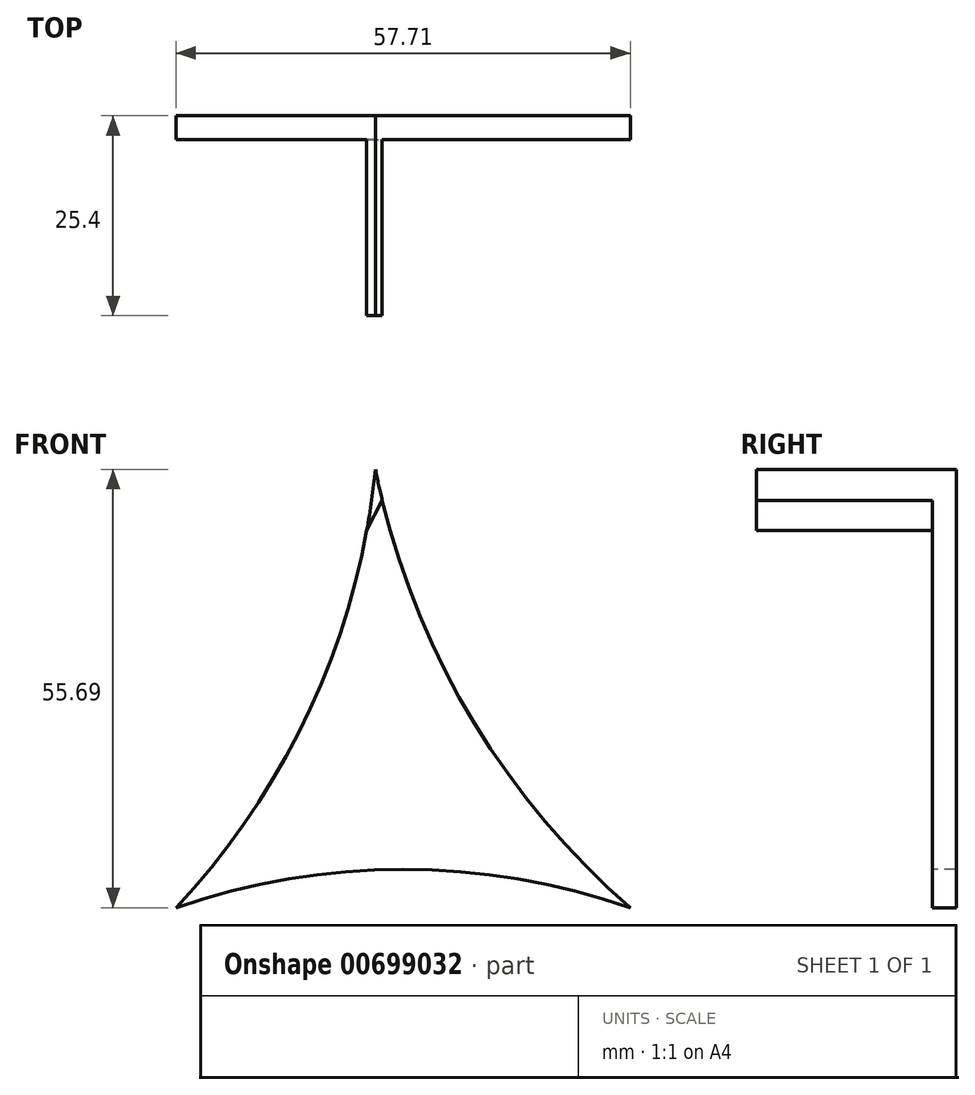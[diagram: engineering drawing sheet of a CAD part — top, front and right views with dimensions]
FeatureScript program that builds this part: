
annotation { "Feature Type Name" : "Feature", "Feature Type Description" : "" }
export const myFeature = defineFeature(function(context is Context, id is Id, definition is map)
    precondition{}
    {
        {
            var Q0;
            Q0=qCreatedBy(makeId("Front.planeOp"),FACE);
            var sketch = newSketch(context, id + "F0", { "sketchPlane" : qUnion([Q0])});
            skLineSegment(sketch, "E0", {"start": v(0, 0) * mm, "end": v(-58, 0) * mm});
            skLineSegment(sketch, "E1", {"start": v(-58, 0) * mm, "end": v(-29.79, 55.11) * mm});
            skLineSegment(sketch, "E2", {"start": v(-29.79, 55.11) * mm, "end": v(0, 0) * mm});
            skSolve(sketch);
        }
        {
            var Q0;
            Q0 = qSketchRegion(id + "F0", true);
            extrude(context, id + "F1", {"entities" : qUnion([Q0]), "depth" : 25.4 * mm, "offsetDistance" : 25.4 * mm});
        }
        {
            var Q0;
            Q0=makeQuery(id+"F0.imprint","IMPRINT",FACE,{"disambiguationData":[TD([[makeQuery(id+"F0.imprint","IMPRINT",EDGE,{"derivedFrom":sQuery(id+"F0.wireOp",EDGE,"E0")}),-1.0]])]});
            var sketch = newSketch(context, id + "F2", { "sketchPlane" : qUnion([Q0])});
            skArc(sketch, "E3", {"start": v(-57.7, 0) * mm, "mid": v(-40.44, 25.75) * mm, "end": v(-32.38, 55.7) * mm});
            skArc(sketch, "E4", {"start": v(-32.38, 55.7) * mm, "mid": v(-20.83, 25.15) * mm, "end": v(0, 0) * mm});
            skArc(sketch, "E5", {"start": v(0, 0) * mm, "mid": v(-28.85, 4.87) * mm, "end": v(-57.7, 0) * mm});
            skSolve(sketch);
        }
        {
            var Q0;
            Q0 = qSketchRegion(id + "F2", true);
            extrude(context, id + "F3", {"entities" : qUnion([Q0]), "operationType" : NewBodyOperationType.ADD, "oppositeDirection" : true, "depth" : 25.4 * mm, "offsetDistance" : 25.4 * mm});
        }
        {
            var Q0;
            {var subQ0=sQuery(id+"F0.wireOp",EDGE,"E2");var subQ1=sQuery(id+"F0.wireOp",EDGE,"E1");var subQ2=sQuery(id+"F0.wireOp",EDGE,"E0");var subQ3=makeQuery(id+"F1.opExtrude","CAP_FACE",FACE,{"disambiguationData":[OSD([subQ2,subQ1,subQ0])],"isStart":true});Q0=makeQuery(id+"F3.boolean.opBoolean","SPLIT",FACE,{"disambiguationData":[TD([makeQuery(id+"F1.opExtrude","SWEPT_FACE",FACE,{"disambiguationData":[OSD([subQ2])]}),subQ3,makeQuery(id+"F1.opExtrude","SWEPT_FACE",FACE,{"disambiguationData":[OSD([subQ1])]}),makeQuery(id+"F1.opExtrude","SWEPT_FACE",FACE,{"disambiguationData":[OSD([subQ0])]}),makeQuery(id+"F3.opExtrude","SWEPT_FACE",FACE,{"disambiguationData":[OSD([sQuery(id+"F2.wireOp",EDGE,"E3")])]}),makeQuery(id+"F3.opExtrude","SWEPT_FACE",FACE,{"disambiguationData":[OSD([sQuery(id+"F2.wireOp",EDGE,"E4")])]}),makeQuery(id+"F3.opExtrude","SWEPT_FACE",FACE,{"disambiguationData":[OSD([sQuery(id+"F2.wireOp",EDGE,"E5")])]})]),OD(0.0)],"derivedFrom":subQ3});}
            var Q1;
            {var subQ0=sQuery(id+"F0.wireOp",EDGE,"E2");var subQ1=sQuery(id+"F0.wireOp",EDGE,"E1");var subQ2=sQuery(id+"F0.wireOp",EDGE,"E0");var subQ3=makeQuery(id+"F1.opExtrude","CAP_FACE",FACE,{"disambiguationData":[OSD([subQ2,subQ1,subQ0])],"isStart":true});Q1=makeQuery(id+"F3.boolean.opBoolean","SPLIT",FACE,{"disambiguationData":[TD([makeQuery(id+"F1.opExtrude","SWEPT_FACE",FACE,{"disambiguationData":[OSD([subQ2])]}),subQ3,makeQuery(id+"F1.opExtrude","SWEPT_FACE",FACE,{"disambiguationData":[OSD([subQ1])]}),makeQuery(id+"F1.opExtrude","SWEPT_FACE",FACE,{"disambiguationData":[OSD([subQ0])]}),makeQuery(id+"F3.opExtrude","SWEPT_FACE",FACE,{"disambiguationData":[OSD([sQuery(id+"F2.wireOp",EDGE,"E3")])]}),makeQuery(id+"F3.opExtrude","SWEPT_FACE",FACE,{"disambiguationData":[OSD([sQuery(id+"F2.wireOp",EDGE,"E4")])]}),makeQuery(id+"F3.opExtrude","SWEPT_FACE",FACE,{"disambiguationData":[OSD([sQuery(id+"F2.wireOp",EDGE,"E5")])]})]),OD(1.0)],"derivedFrom":subQ3});}
            var Q2;
            {var subQ0=sQuery(id+"F0.wireOp",EDGE,"E2");var subQ1=sQuery(id+"F0.wireOp",EDGE,"E0");var subQ2=makeQuery(id+"F1.opExtrude","CAP_FACE",FACE,{"disambiguationData":[OSD([subQ1,sQuery(id+"F0.wireOp",EDGE,"E1"),subQ0])],"isStart":true});Q2=makeQuery(id+"F3.boolean.opBoolean","SPLIT",FACE,{"disambiguationData":[TD([makeQuery(id+"F1.opExtrude","SWEPT_FACE",FACE,{"disambiguationData":[OSD([subQ1])]}),subQ2,makeQuery(id+"F1.opExtrude","SWEPT_FACE",FACE,{"disambiguationData":[OSD([subQ0])]}),makeQuery(id+"F3.opExtrude","SWEPT_FACE",FACE,{"disambiguationData":[OSD([sQuery(id+"F2.wireOp",EDGE,"E3")])]}),makeQuery(id+"F3.opExtrude","SWEPT_FACE",FACE,{"disambiguationData":[OSD([sQuery(id+"F2.wireOp",EDGE,"E4")])]}),makeQuery(id+"F3.opExtrude","SWEPT_FACE",FACE,{"disambiguationData":[OSD([sQuery(id+"F2.wireOp",EDGE,"E5")])]})])],"derivedFrom":subQ2});}
            extrude(context, id + "F4", {"entities" : qUnion([Q0, Q1, Q2]), "operationType" : NewBodyOperationType.REMOVE, "oppositeDirection" : true, "depth" : 25.4 * mm, "offsetDistance" : 25.4 * mm});
        }
        {
            var Q0;
            Q0=makeQuery(id+"F1.opExtrude","CAP_FACE",FACE,{"disambiguationData":[OSD([sQuery(id+"F0.wireOp",EDGE,"E0"),sQuery(id+"F0.wireOp",EDGE,"E1"),sQuery(id+"F0.wireOp",EDGE,"E2")])],"isStart":false});
            extrude(context, id + "F5", {"entities" : qUnion([Q0]), "operationType" : NewBodyOperationType.REMOVE, "oppositeDirection" : true, "depth" : 47.75 * mm, "offsetDistance" : 25.4 * mm});
        }
    });
